# Revit family: EKF_EE_ВертикальныйПрофильДляВРУUnitS-R-ЩО-70_PROxima
name_source: partatom
category: Электрооборудование
units: mm (PartAtom-declared; Revit-internal decimal feet)

## family parameters
Всегда вертикально = Нет
На основе рабочей плоскости = Да
Общий = Да
При загрузке вырезать с полостями = Нет
Размер круглого соединителя = Использовать диаметр
Тип детали = Силовой щит
Точка расчета площади = Нет

## types (2) — shared parameters
ADSK_Единица измерения = шт.
ADSK_Завод-изготовитель = EKF
ADSK_Количество = 1
ADSK_Марка = Вертикальный профиль
ADSK_Материал = Сталь_Оцинкованная
ADSK_Обозначение = Вертикальный профиль
ADSK_Размер_Глубина = 40 мм
ADSK_Размер_Ширина = 40 мм
a = 40 мм
t = 1.2 мм
Изготовитель = EKF
Серия номенклатуры = Unit PROxima
Степень защиты IP = -
ТВ = EKF_2
Тип установки = -
Шаг = 35 мм
zero-valued in all types: ADSK_Масса, Отметка по умолчанию

## per-type parameters (varying)
| type | ADSK_Код изделия | ADSK_Размер_Высота | Отступ | Тип |
| Вертикальный профиль для ВРУ Unit S и R и ЩО-70 (1800хШхГ) EKF PROxima | mb15-07-02 | 1600 мм | 30 мм | 13 мм |
| Вертикальный профиль для ВРУ Unit S и R и ЩО-70 (2000хШхГ) EKF PROxima | mb15-04-05 | 1800 мм | 25 мм | 14 мм |

note: column(s) folded — value = type name in every type: ADSK_Наименование
